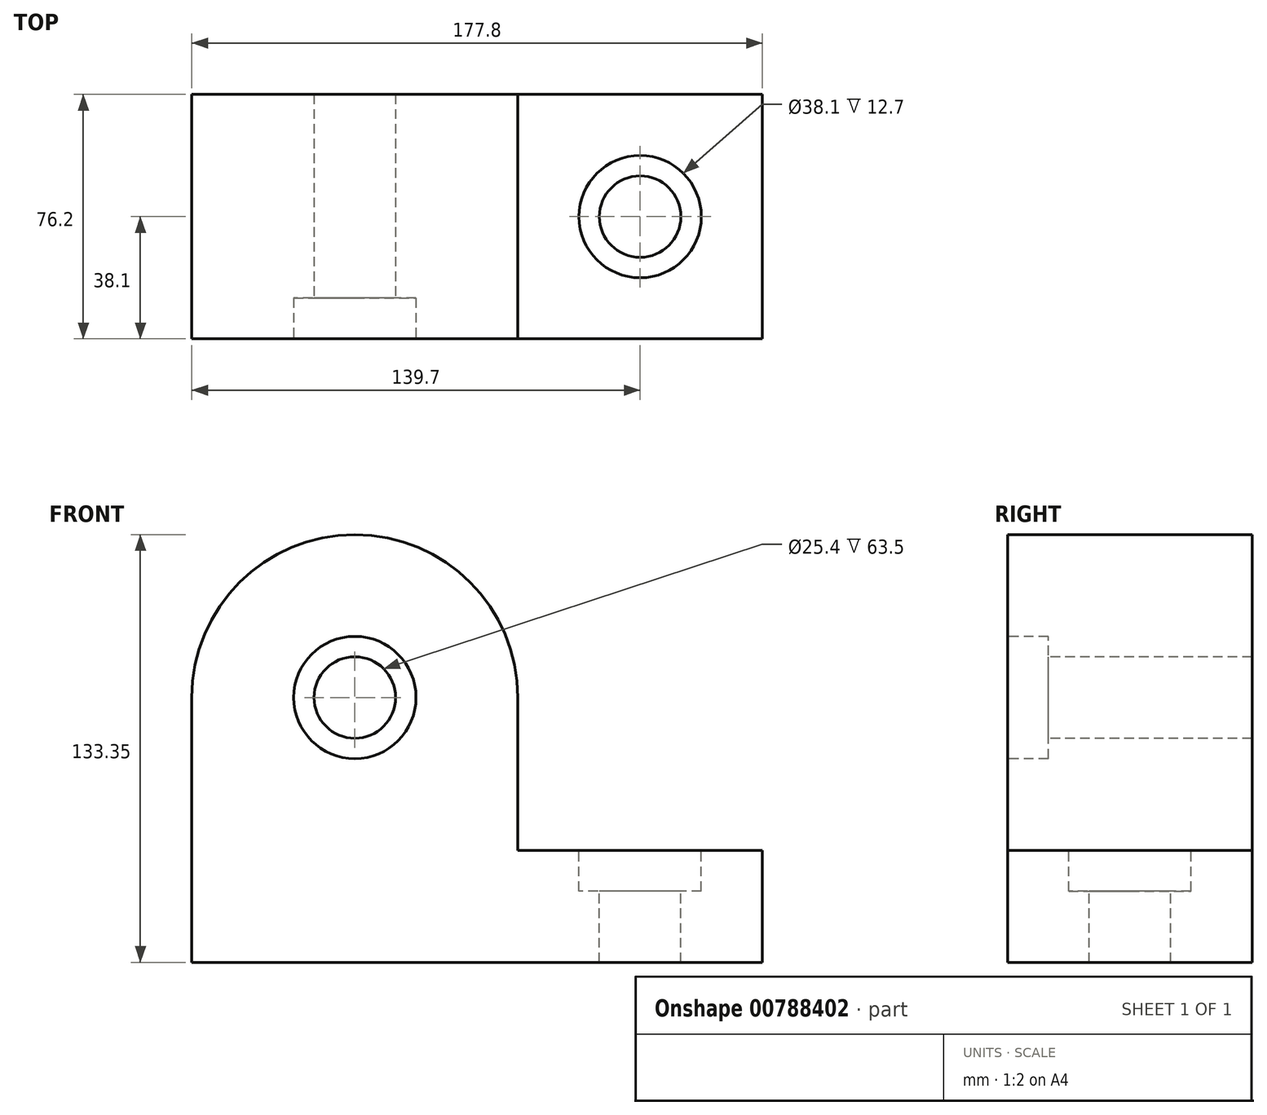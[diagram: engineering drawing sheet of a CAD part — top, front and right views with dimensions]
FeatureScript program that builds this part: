
annotation { "Feature Type Name" : "Feature", "Feature Type Description" : "" }
export const myFeature = defineFeature(function(context is Context, id is Id, definition is map)
    precondition{}
    {
        {
            var Q0;
            Q0=qCreatedBy(makeId("Front.planeOp"),FACE);
            var sketch = newSketch(context, id + "F0", { "sketchPlane" : qUnion([Q0])});
            skLineSegment(sketch, "E0", {"start": v(0, 0) * mm, "end": v(177.8, 0) * mm});
            skLineSegment(sketch, "E1", {"start": v(177.8, 0) * mm, "end": v(177.8, 34.93) * mm});
            skLineSegment(sketch, "E2", {"start": v(177.8, 34.93) * mm, "end": v(101.6, 34.93) * mm});
            skLineSegment(sketch, "E3", {"start": v(101.6, 34.93) * mm, "end": v(101.6, 82.55) * mm});
            skLineSegment(sketch, "E4", {"start": v(101.6, 82.55) * mm, "end": v(0, 82.55) * mm, "construction": true});
            skLineSegment(sketch, "E5", {"start": v(0, 82.55) * mm, "end": v(0, 0) * mm});
            skArc(sketch, "E6", {"start": v(101.6, 82.55) * mm, "mid": v(50.8, 133.35) * mm, "end": v(0, 82.55) * mm});
            skSolve(sketch);
        }
        {
            var Q0;
            Q0=makeQuery(id+"F0.imprint","IMPRINT",FACE,{"disambiguationData":[TD([[makeQuery(id+"F0.imprint","IMPRINT",EDGE,{"derivedFrom":sQuery(id+"F0.wireOp",EDGE,"E0")}),1.0]])]});
            extrude(context, id + "F1", {"entities" : qUnion([Q0]), "depth" : 76.2 * mm, "offsetDistance" : 25.4 * mm});
        }
        {
            var Q0;
            Q0=makeQuery(id+"F1.opExtrude","CAP_FACE",FACE,{"disambiguationData":[OSD([sQuery(id+"F0.wireOp",EDGE,"E0"),sQuery(id+"F0.wireOp",EDGE,"E1"),sQuery(id+"F0.wireOp",EDGE,"E2"),sQuery(id+"F0.wireOp",EDGE,"E3"),sQuery(id+"F0.wireOp",EDGE,"E5"),sQuery(id+"F0.wireOp",EDGE,"E6")])],"isStart":false});
            var sketch = newSketch(context, id + "F2", { "sketchPlane" : qUnion([Q0])});
            skLineSegment(sketch, "E7", {"start": v(0, 82.55) * mm, "end": v(101.6, 82.55) * mm, "construction": true});
            skCircle(sketch, "E8", {"center": v(50.8, 82.55) * mm, "radius": 19.05 * mm});
            skSolve(sketch);
        }
        {
            var Q0;
            Q0=makeQuery(id+"F2.imprint","IMPRINT",FACE,{"disambiguationData":[TD([[makeQuery(id+"F2.imprint","IMPRINT",EDGE,{"derivedFrom":sQuery(id+"F2.wireOp",EDGE,"E8")}),1.0]])]});
            extrude(context, id + "F3", {"entities" : qUnion([Q0]), "operationType" : NewBodyOperationType.REMOVE, "oppositeDirection" : true, "depth" : 12.7 * mm, "offsetDistance" : 25.4 * mm});
        }
        {
            var Q0;
            Q0=makeQuery(id+"F1.opExtrude","CAP_FACE",FACE,{"disambiguationData":[OSD([sQuery(id+"F0.wireOp",EDGE,"E0"),sQuery(id+"F0.wireOp",EDGE,"E1"),sQuery(id+"F0.wireOp",EDGE,"E2"),sQuery(id+"F0.wireOp",EDGE,"E3"),sQuery(id+"F0.wireOp",EDGE,"E5"),sQuery(id+"F0.wireOp",EDGE,"E6")])],"isStart":false});
            var sketch = newSketch(context, id + "F4", { "sketchPlane" : qUnion([Q0])});
            skLineSegment(sketch, "E9", {"start": v(0, 82.55) * mm, "end": v(101.6, 82.55) * mm, "construction": true});
            skCircle(sketch, "E10", {"center": v(50.8, 82.55) * mm, "radius": 12.7 * mm});
            skSolve(sketch);
        }
        {
            var Q0;
            Q0=makeQuery(id+"F4.imprint","IMPRINT",FACE,{"disambiguationData":[TD([[makeQuery(id+"F4.imprint","IMPRINT",EDGE,{"derivedFrom":sQuery(id+"F4.wireOp",EDGE,"E10")}),1.0]])]});
            extrude(context, id + "F5", {"entities" : qUnion([Q0]), "operationType" : NewBodyOperationType.REMOVE, "endBound" : BoundingType.THROUGH_ALL, "oppositeDirection" : true, "depth" : 25.4 * mm, "offsetDistance" : 25.4 * mm});
        }
        {
            var Q0;
            Q0=makeQuery(id+"F1.opExtrude","SWEPT_FACE",FACE,{"disambiguationData":[OSD([sQuery(id+"F0.wireOp",EDGE,"E2")])]});
            var sketch = newSketch(context, id + "F6", { "sketchPlane" : qUnion([Q0])});
            skLineSegment(sketch, "E11", {"start": v(177.8, -38.1) * mm, "end": v(101.6, -38.1) * mm, "construction": true});
            skCircle(sketch, "E12", {"center": v(139.7, -38.1) * mm, "radius": 19.05 * mm});
            skSolve(sketch);
        }
        {
            var Q0;
            Q0=makeQuery(id+"F6.imprint","IMPRINT",FACE,{"disambiguationData":[TD([[makeQuery(id+"F6.imprint","IMPRINT",EDGE,{"derivedFrom":sQuery(id+"F6.wireOp",EDGE,"E12")}),1.0]])]});
            extrude(context, id + "F7", {"entities" : qUnion([Q0]), "operationType" : NewBodyOperationType.REMOVE, "oppositeDirection" : true, "depth" : 12.7 * mm, "offsetDistance" : 25.4 * mm});
        }
        {
            var Q0;
            Q0=makeQuery(id+"F1.opExtrude","SWEPT_FACE",FACE,{"disambiguationData":[OSD([sQuery(id+"F0.wireOp",EDGE,"E2")])]});
            var sketch = newSketch(context, id + "F8", { "sketchPlane" : qUnion([Q0])});
            skLineSegment(sketch, "E13", {"start": v(101.6, -38.1) * mm, "end": v(177.8, -38.1) * mm, "construction": true});
            skCircle(sketch, "E14", {"center": v(139.7, -38.1) * mm, "radius": 12.7 * mm});
            skSolve(sketch);
        }
        {
            var Q0;
            Q0=makeQuery(id+"F8.imprint","IMPRINT",FACE,{"disambiguationData":[TD([[makeQuery(id+"F8.imprint","IMPRINT",EDGE,{"derivedFrom":sQuery(id+"F8.wireOp",EDGE,"E14")}),1.0]])]});
            extrude(context, id + "F9", {"entities" : qUnion([Q0]), "operationType" : NewBodyOperationType.REMOVE, "endBound" : BoundingType.THROUGH_ALL, "oppositeDirection" : true, "depth" : 25.4 * mm, "offsetDistance" : 25.4 * mm});
        }
    });
